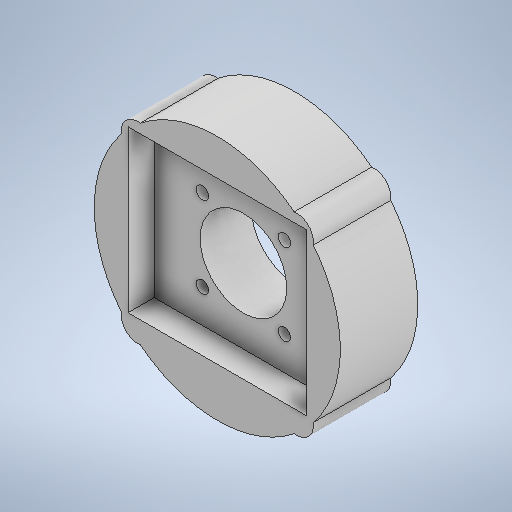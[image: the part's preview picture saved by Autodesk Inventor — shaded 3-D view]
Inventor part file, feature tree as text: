
AUTODESK INVENTOR PART (.ipt)
format: ipt  version: 2025.1 (Build 291241000, 241)  size: 330,752 bytes
history: native  units: mm
features: sketch x6, extrude x5
ambient origin geometry x8: Origin, YZ Plane, XZ Plane, XY Plane, X Axis, Y Axis, Z Axis, Center Point
bodies: Solid1 (feature_tree)
feature tree (11):
  extrude  "Extrusion1"  Depth=10.0mm
  extrude  "Extrusion6"  Depth=70.05mm
  extrude  "Extrusion7"  Depth=74.060786mm
  extrude  "Extrusion8"  Depth=21.9mm TaperAngle=0.0deg
  extrude  "Extrusion9"  TaperAngle=0.0deg  [1 undecoded]
  sketch  "Sketch1"  dims[d0=10.0mm d1=0.25mm]
  sketch  "Skizze - Runde Anordnung1"  dims[d2=40.0mm d4=360.0deg d6=70.05mm]
  sketch  "Skizze6"  dims[d7=0.25mm d8=74.060786mm]
  sketch  "Skizze7"  dims[d9=73.5mm d10=21.9mm d11=0.0mm]
  sketch  "Skizze8"  dims[d33=24.45mm d34=0.0mm d35=0.0mm]
  sketch  "Skizze9"  dims[d38=7.4mm d39=0.0mm d40=23.14mm d41=23.14mm d42=3.5mm d43=3.5mm d44=3.5mm d45=3.5mm d46=0.0mm d47=0.0mm d48=1.75mm d49=50.46mm d50=45.54mm d51=6.2mm d52=6.2mm d53=6.2mm d54=6.2mm d55=3.5mm d56=0.0mm d30=0.5mm d31=0.872665mm d32=0.5mm]
note: 1 required parameter value undecoded (feature->parameter linkage not recoverable at this tier; creation-order binding heuristic only, values carry confidence <= 0.55)
